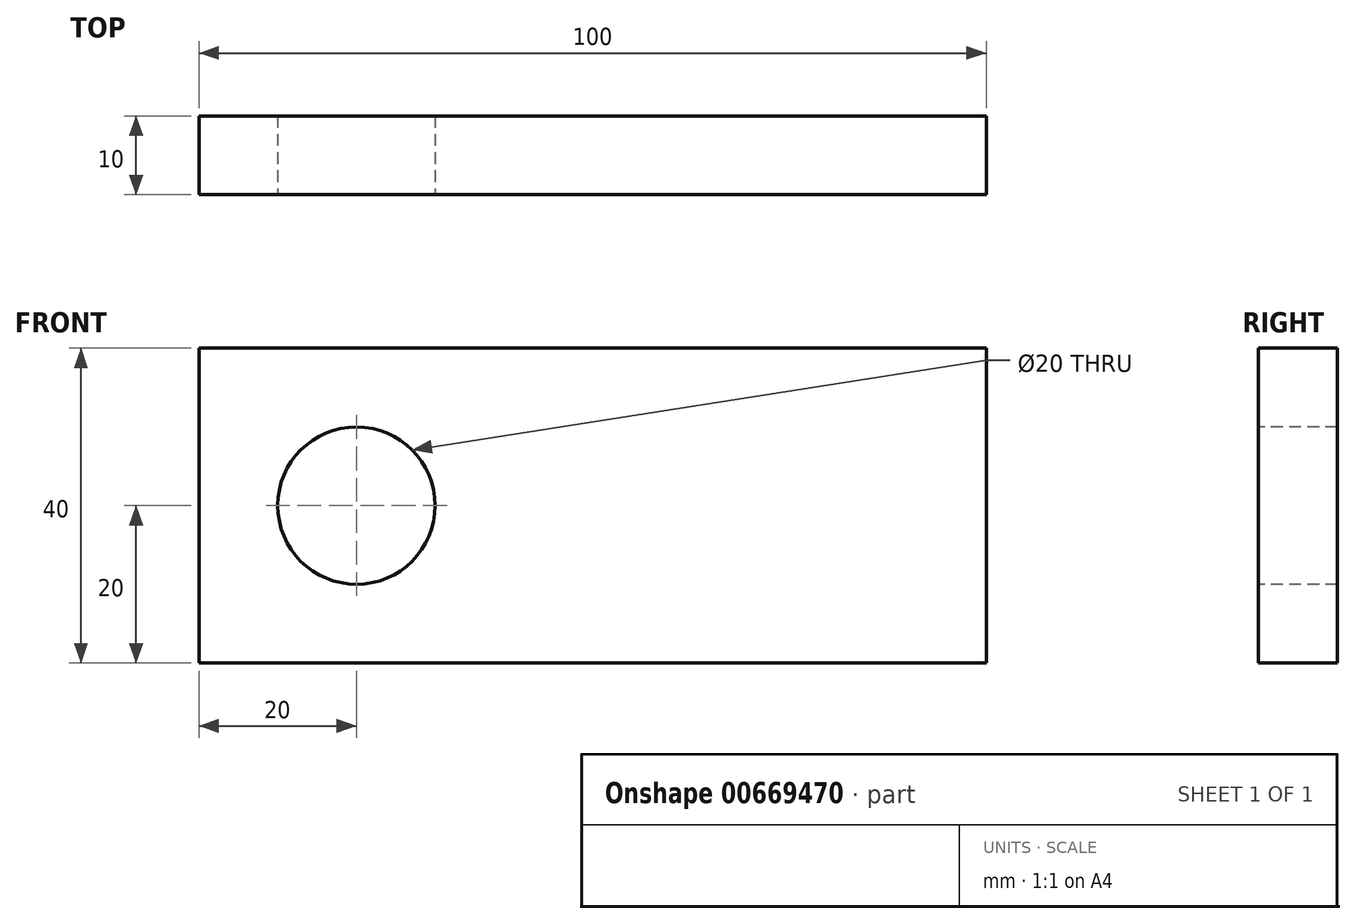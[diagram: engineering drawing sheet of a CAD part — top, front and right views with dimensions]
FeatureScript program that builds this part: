
annotation { "Feature Type Name" : "Feature", "Feature Type Description" : "" }
export const myFeature = defineFeature(function(context is Context, id is Id, definition is map)
    precondition{}
    {
        {
            var Q0;
            Q0=qCreatedBy(makeId("Front.planeOp"),FACE);
            var sketch = newSketch(context, id + "F0", { "sketchPlane" : qUnion([Q0])});
            skLineSegment(sketch, "E0", {"start": v(0, 0) * mm, "end": v(-100, 0) * mm});
            skLineSegment(sketch, "E1", {"start": v(-100, 0) * mm, "end": v(-100, 40) * mm});
            skLineSegment(sketch, "E2", {"start": v(-100, 40) * mm, "end": v(0, 40) * mm});
            skLineSegment(sketch, "E3", {"start": v(0, 40) * mm, "end": v(0, 0) * mm});
            skCircle(sketch, "E4", {"center": v(-80, 20) * mm, "radius": 10 * mm});
            skSolve(sketch);
        }
        {
            var Q0;
            Q0=makeQuery(id+"F0.imprint","IMPRINT",FACE,{"disambiguationData":[TD([[makeQuery(id+"F0.imprint","IMPRINT",EDGE,{"derivedFrom":sQuery(id+"F0.wireOp",EDGE,"E0")}),-1.0]])]});
            extrude(context, id + "F1", {"entities" : qUnion([Q0]), "endBound" : BoundingType.SYMMETRIC, "oppositeDirection" : true, "depth" : 10 * mm, "offsetDistance" : 25 * mm});
        }
    });
